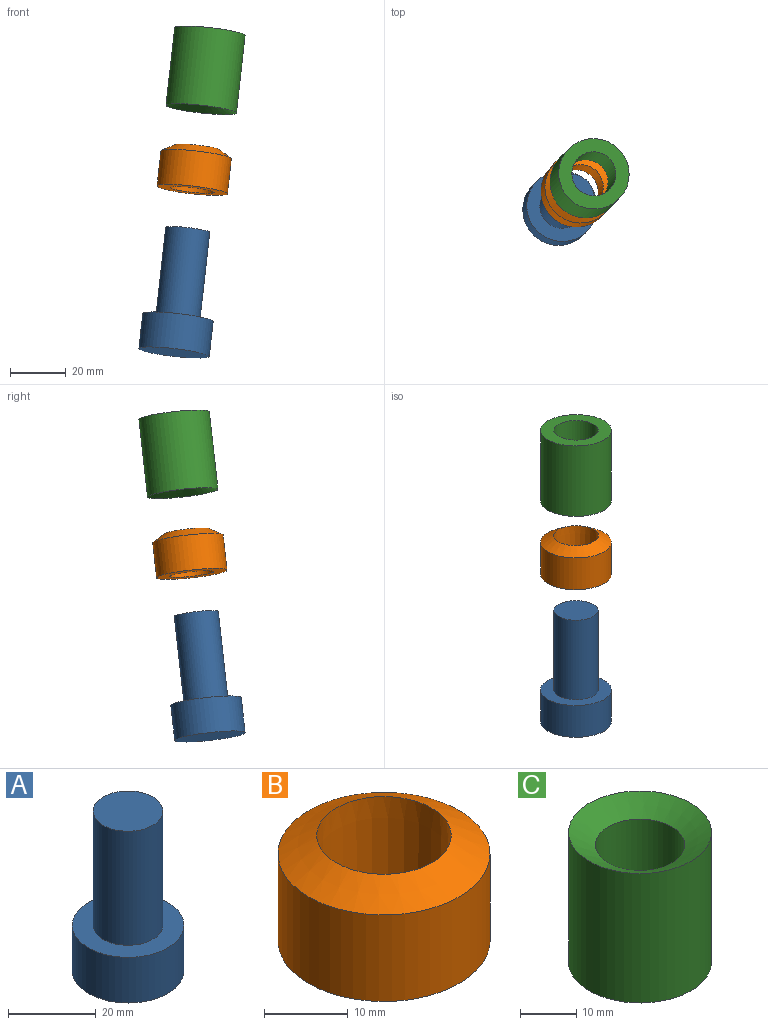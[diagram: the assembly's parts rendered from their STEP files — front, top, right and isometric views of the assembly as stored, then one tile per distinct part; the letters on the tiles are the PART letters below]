
ASSEMBLY  parts=3 mates=2
PART A: 5 faces, bbox 25.4x25.4x44.5 mm
  f0: plane 25.4x25.4mm, normal (0,0,-1), area 506.7mm2, adj f1
  f1: cylinder r=12.7mm len=25.4mm, axis (0,0,1), area 1013.4mm2, adj f0,f2
  f2: plane 25.4x25.4mm, normal (0,0,1), area 308.8mm2, adj f1,f3
  f3: cylinder r=7.94mm len=31.75mm, axis (0,0,1), area 1583.5mm2, adj f2,f4
  f4: plane 15.88x15.88mm, normal (0,0,1), area 197.9mm2, adj f3
PART B: 4 faces, bbox 25.4x25.4x15.4 mm
  f0: cone r=7.94mm half-angle=0.4deg, axis (0,0,1), area 772.8mm2, adj f1,f3
  f1: plane 25.4x25.4mm, normal (0,0,-1), area 308.8mm2, adj f0,f2
  f2: cylinder r=12.7mm len=25.4mm, axis (0,0,-1), area 1013.4mm2, adj f1,f3
  f3: cone r=12.7mm half-angle=60deg, axis (0,0,-1), area 349.9mm2, adj f0,f2
PART C: 4 faces, bbox 25.4x25.4x28.1 mm
  f0: cylinder r=7.94mm len=25.4mm, axis (0,0,1), area 1266.8mm2, adj f1,f3
  f1: plane 25.4x25.4mm, normal (0,0,-1), area 308.8mm2, adj f0,f2
  f2: cylinder r=12.7mm len=28.15mm, axis (0,0,1), area 2246.2mm2, adj f1,f3
  f3: cone r=12.7mm half-angle=60deg, axis (0,0,1), area 356.5mm2, adj f0,f2
PLACE A rot(axis=(-0.71,0.7,-0.06),9deg) t=(-81.21,21.3,-106.67)mm
PLACE B rot(axis=(0,0.11,0.99),89.8deg) t=(-74.7,27.81,-48.39)mm
PLACE C rot(axis=(1,-0.01,-0.06),173.6deg) t=(-68.37,34.14,8.38)mm
MATE cylindrical B.f0 <-> A.f1  axis (0.11,0.11,0.99) through (-73.01,29.5,-33.2)mm
MATE cylindrical B.f0 <-> C.f0  axis (0.11,0.11,0.99) through (-73.01,29.5,-33.2)mm
